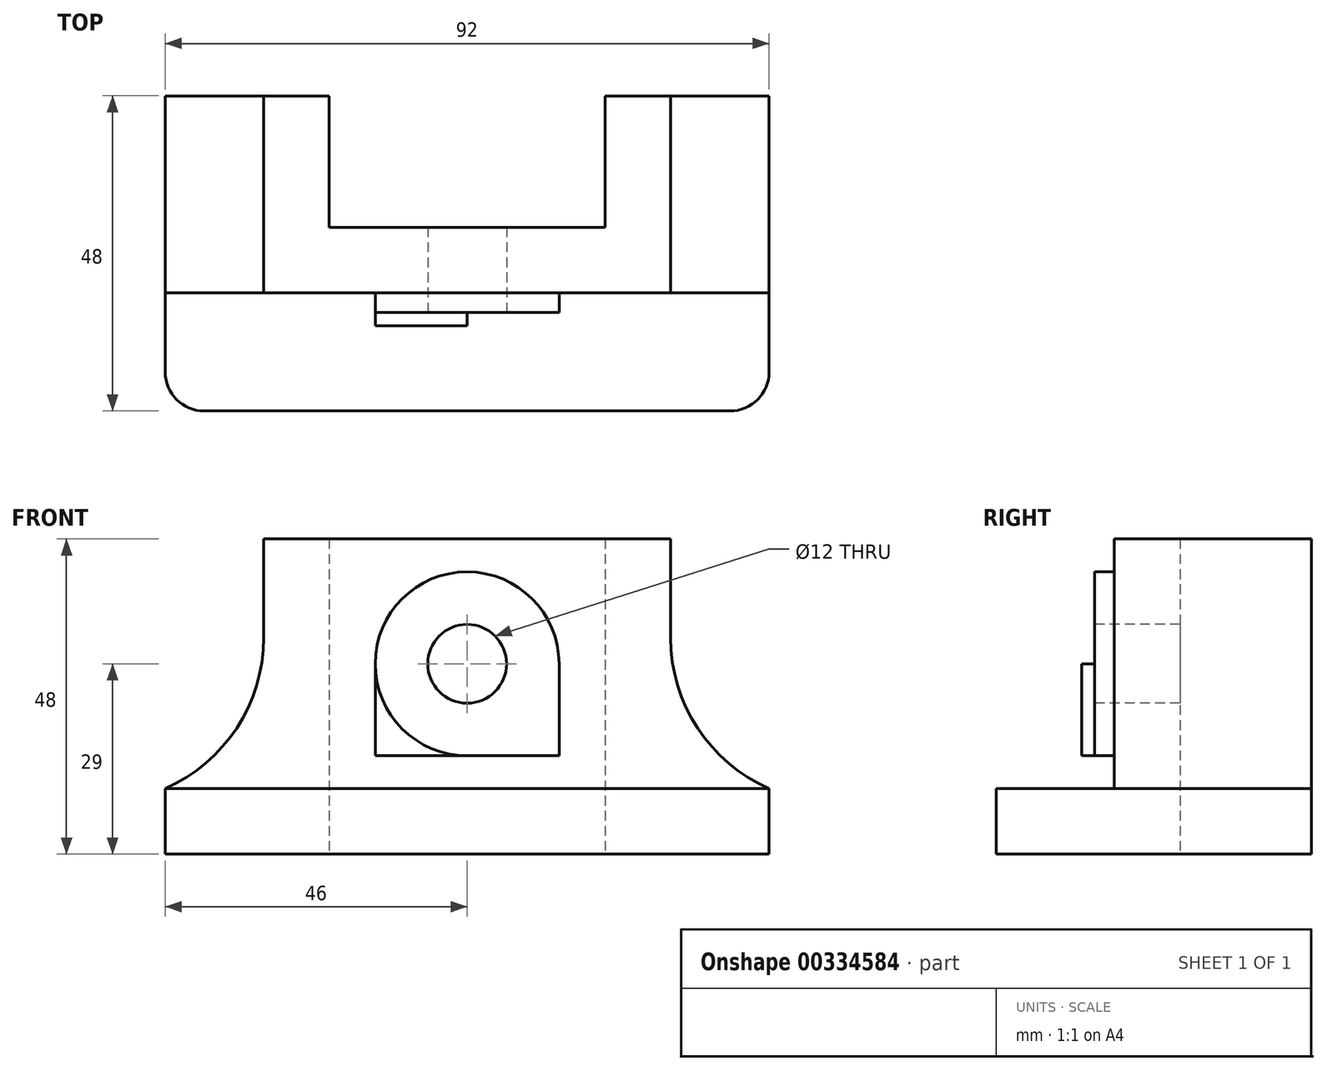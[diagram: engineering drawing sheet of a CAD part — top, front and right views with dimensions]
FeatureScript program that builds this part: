
annotation { "Feature Type Name" : "Feature", "Feature Type Description" : "" }
export const myFeature = defineFeature(function(context is Context, id is Id, definition is map)
    precondition{}
    {
        {
            var Q0;
            Q0=qCreatedBy(makeId("Top.planeOp"),FACE);
            var sketch = newSketch(context, id + "F0", { "sketchPlane" : qUnion([Q0])});
            skLineSegment(sketch, "E0.bottom", {"start": v(-46, 29.82) * mm, "end": v(46, 29.82) * mm});
            skLineSegment(sketch, "E0.top", {"start": v(-46, -18.18) * mm, "end": v(46, -18.18) * mm});
            skLineSegment(sketch, "E0.left", {"start": v(-46, 29.82) * mm, "end": v(-46, -18.18) * mm});
            skLineSegment(sketch, "E0.right", {"start": v(46, 29.82) * mm, "end": v(46, -18.18) * mm});
            skLineSegment(sketch, "E1.bottom", {"start": v(-21, 33.48) * mm, "end": v(21, 33.48) * mm});
            skLineSegment(sketch, "E1.top", {"start": v(-21, 9.82) * mm, "end": v(21, 9.82) * mm});
            skLineSegment(sketch, "E1.left", {"start": v(-21, 33.48) * mm, "end": v(-21, 9.82) * mm});
            skLineSegment(sketch, "E1.right", {"start": v(21, 33.48) * mm, "end": v(21, 9.82) * mm});
            skLineSegment(sketch, "E2", {"start": v(-46, -0.18) * mm, "end": v(46, -0.18) * mm});
            skLineSegment(sketch, "E3", {"start": v(-31, 29.82) * mm, "end": v(-31, 0) * mm});
            skLineSegment(sketch, "E4", {"start": v(31, 29.82) * mm, "end": v(31, 0) * mm});
            skSolve(sketch);
        }
        {
            var Q0;
            {var subQ5=sQuery(id+"F0.wireOp",EDGE,"E1.top");Q0=makeQuery(id+"F0.imprint","IMPRINT",FACE,{"disambiguationData":[TD([[makeQuery(id+"F0.imprint","IMPRINT",EDGE,{"derivedFrom":subQ5}),-1.0]])]});}
            extrude(context, id + "F1", {"entities" : qUnion([Q0]), "depth" : 48 * mm});
        }
        {
            var Q0;
            {var subQ0=sQuery(id+"F0.wireOp",EDGE,"E0.top");Q0=makeQuery(id+"F0.imprint","IMPRINT",FACE,{"disambiguationData":[TD([[makeQuery(id+"F0.imprint","IMPRINT",EDGE,{"derivedFrom":subQ0}),1.0]])]});}
            extrude(context, id + "F2", {"entities" : qUnion([Q0]), "operationType" : NewBodyOperationType.ADD, "depth" : 10 * mm});
        }
        {
            var Q0;
            Q0=makeQuery(id+"F1.opExtrude","SWEPT_FACE",FACE,{"disambiguationData":[OSD([sQuery(id+"F0.wireOp",EDGE,"E2")])]});
            var sketch = newSketch(context, id + "F3", { "sketchPlane" : qUnion([Q0])});
            skLineSegment(sketch, "E5", {"start": v(-31, 48) * mm, "end": v(-31, 10) * mm});
            skCircle(sketch, "E6", {"center": v(-56, 32.91) * mm, "radius": 25 * mm});
            skLineSegment(sketch, "E7", {"start": v(31, 48) * mm, "end": v(31, 10) * mm});
            skCircle(sketch, "E8", {"center": v(56, 32.91) * mm, "radius": 25 * mm});
            skSolve(sketch);
        }
        {
            var Q0;
            {var subQ2=sQuery(id+"F0.wireOp",EDGE,"E2");var subQ5=makeQuery(id+"F1.opExtrude","SWEPT_EDGE",EDGE,{"disambiguationData":[OSD([sQuery(id+"F0.wireOp",EDGE,"E0.left"),subQ2])]});Q0=makeQuery(id+"F3.imprint","IMPRINT",FACE,{"disambiguationData":[TD([[makeQuery(id+"F3.imprint","IMPRINT",EDGE,{"derivedFrom":subQ5}),1.0]])]});}
            var Q1;
            {var subQ0=sQuery(id+"F3.wireOp",EDGE,"E5");var subQ1=makeQuery(id+"F1.opExtrude","CAP_EDGE",EDGE,{"disambiguationData":[OSD([sQuery(id+"F0.wireOp",EDGE,"E2")])],"isStart":false});var subQ2=makeQuery(id+"F3.imprint","INTERSECT",VERTEX,{"derivedFrom":[subQ1,subQ0]});Q1=makeQuery(id+"F3.imprint","IMPRINT",FACE,{"disambiguationData":[TD([[makeQuery(id+"F3.imprint","IMPRINT",EDGE,{"disambiguationData":[TD([[subQ2,-1.0]])],"derivedFrom":subQ0}),-1.0]])]});}
            var Q2;
            {var subQ2=sQuery(id+"F0.wireOp",EDGE,"E2");var subQ5=makeQuery(id+"F1.opExtrude","SWEPT_EDGE",EDGE,{"disambiguationData":[OSD([sQuery(id+"F0.wireOp",EDGE,"E0.right"),subQ2])]});Q2=makeQuery(id+"F3.imprint","IMPRINT",FACE,{"disambiguationData":[TD([[makeQuery(id+"F3.imprint","IMPRINT",EDGE,{"derivedFrom":subQ5}),-1.0]])]});}
            var Q3;
            {var subQ0=sQuery(id+"F3.wireOp",EDGE,"E7");var subQ1=makeQuery(id+"F1.opExtrude","CAP_EDGE",EDGE,{"disambiguationData":[OSD([sQuery(id+"F0.wireOp",EDGE,"E2")])],"isStart":false});var subQ2=makeQuery(id+"F3.imprint","INTERSECT",VERTEX,{"derivedFrom":[subQ1,subQ0]});Q3=makeQuery(id+"F3.imprint","IMPRINT",FACE,{"disambiguationData":[TD([[makeQuery(id+"F3.imprint","IMPRINT",EDGE,{"disambiguationData":[TD([[subQ2,-1.0]])],"derivedFrom":subQ0}),1.0]])]});}
            extrude(context, id + "F4", {"entities" : qUnion([Q0, Q1, Q2, Q3]), "operationType" : NewBodyOperationType.REMOVE, "oppositeDirection" : true, "depth" : 63 * mm});
        }
        {
            var Q0;
            Q0=makeQuery(id+"F1.opExtrude","SWEPT_FACE",FACE,{"disambiguationData":[OSD([sQuery(id+"F0.wireOp",EDGE,"E2")])]});
            var sketch = newSketch(context, id + "F5", { "sketchPlane" : qUnion([Q0])});
            skCircle(sketch, "E9", {"center": v(0, 29) * mm, "radius": 14 * mm});
            skLineSegment(sketch, "E10", {"start": v(0, 29) * mm, "end": v(-14, 29) * mm});
            skLineSegment(sketch, "E11", {"start": v(-14, 29) * mm, "end": v(-14, 10) * mm});
            skLineSegment(sketch, "E12", {"start": v(0, 29) * mm, "end": v(14, 29) * mm});
            skLineSegment(sketch, "E13", {"start": v(14, 29) * mm, "end": v(14, 10) * mm});
            skLineSegment(sketch, "E14", {"start": v(-14, 15) * mm, "end": v(14, 15) * mm});
            skSolve(sketch);
        }
        {
            var Q0;
            {var subQ1=sQuery(id+"F5.wireOp",EDGE,"E11");var subQ5=makeQuery(id+"F2.opExtrude","CAP_EDGE",EDGE,{"disambiguationData":[OSD([sQuery(id+"F0.wireOp",EDGE,"E2")])],"isStart":false});var subQ8=makeQuery(id+"F5.imprint","INTERSECT",VERTEX,{"derivedFrom":[subQ5,subQ1]});Q0=makeQuery(id+"F5.imprint","IMPRINT",FACE,{"disambiguationData":[TD([[makeQuery(id+"F5.imprint","IMPRINT",EDGE,{"disambiguationData":[TD([[subQ8,1.0]])],"derivedFrom":subQ1}),1.0]])]});}
            extrude(context, id + "F6", {"entities" : qUnion([Q0]), "operationType" : NewBodyOperationType.ADD, "depth" : 5 * mm});
        }
        {
            var Q0;
            {var subQ0=sQuery(id+"F5.wireOp",EDGE,"E10");Q0=makeQuery(id+"F5.imprint","IMPRINT",FACE,{"disambiguationData":[TD([[makeQuery(id+"F5.imprint","IMPRINT",EDGE,{"derivedFrom":subQ0}),-1.0]])]});}
            var Q1;
            {var subQ0=sQuery(id+"F5.wireOp",EDGE,"E10");Q1=makeQuery(id+"F5.imprint","IMPRINT",FACE,{"disambiguationData":[TD([[makeQuery(id+"F5.imprint","IMPRINT",EDGE,{"derivedFrom":subQ0}),1.0]])]});}
            var Q2;
            {var subQ0=sQuery(id+"F5.wireOp",EDGE,"E13");var subQ3=sQuery(id+"F5.wireOp",EDGE,"E14");var subQ5=makeQuery(id+"F5.imprint","INTERSECT",VERTEX,{"derivedFrom":[subQ0,subQ3]});Q2=makeQuery(id+"F5.imprint","IMPRINT",FACE,{"disambiguationData":[TD([[makeQuery(id+"F5.imprint","IMPRINT",EDGE,{"disambiguationData":[TD([[subQ5,1.0]])],"derivedFrom":subQ3}),1.0]])]});}
            var Q3;
            {var subQ0=sQuery(id+"F5.wireOp",EDGE,"E11");var subQ3=sQuery(id+"F5.wireOp",EDGE,"E14");var subQ5=makeQuery(id+"F5.imprint","INTERSECT",VERTEX,{"derivedFrom":[subQ0,subQ3]});Q3=makeQuery(id+"F5.imprint","IMPRINT",FACE,{"disambiguationData":[TD([[makeQuery(id+"F5.imprint","IMPRINT",EDGE,{"disambiguationData":[TD([[subQ5,-1.0]])],"derivedFrom":subQ3}),1.0]])]});}
            extrude(context, id + "F7", {"entities" : qUnion([Q0, Q1, Q2, Q3]), "operationType" : NewBodyOperationType.ADD, "depth" : 3 * mm});
        }
        {
            var Q0;
            Q0=makeQuery(id+"F7.opExtrude","CAP_FACE",FACE,{"disambiguationData":[OSD([sQuery(id+"F5.wireOp",EDGE,"E9"),sQuery(id+"F5.wireOp",EDGE,"E11"),sQuery(id+"F5.wireOp",EDGE,"E13"),sQuery(id+"F5.wireOp",EDGE,"E14")])],"isStart":false});
            var sketch = newSketch(context, id + "F8", { "sketchPlane" : qUnion([Q0])});
            skCircle(sketch, "E15", {"center": v(0, 29) * mm, "radius": 6 * mm});
            skSolve(sketch);
        }
        {
            var Q0;
            Q0=makeQuery(id+"F8.imprint","IMPRINT",FACE,{"disambiguationData":[TD([[makeQuery(id+"F8.imprint","IMPRINT",EDGE,{"derivedFrom":sQuery(id+"F8.wireOp",EDGE,"E15")}),1.0]])]});
            extrude(context, id + "F9", {"entities" : qUnion([Q0]), "operationType" : NewBodyOperationType.REMOVE, "oppositeDirection" : true, "depth" : 55.6 * mm});
        }
        {
            var Q0;
            Q0=makeQuery(id+"F2.opExtrude","SWEPT_EDGE",EDGE,{"disambiguationData":[OSD([sQuery(id+"F0.wireOp",EDGE,"E0.top"),sQuery(id+"F0.wireOp",EDGE,"E0.left")])]});
            var Q1;
            Q1=makeQuery(id+"F2.opExtrude","SWEPT_EDGE",EDGE,{"disambiguationData":[OSD([sQuery(id+"F0.wireOp",EDGE,"E0.top"),sQuery(id+"F0.wireOp",EDGE,"E0.right")])]});
            fillet(context, id + "F10", {"entities" : qUnion([Q0, Q1]), "radius" : 6 * mm, "tangentPropagation" : true, "allowEdgeOverflow" : false});
        }
    });
